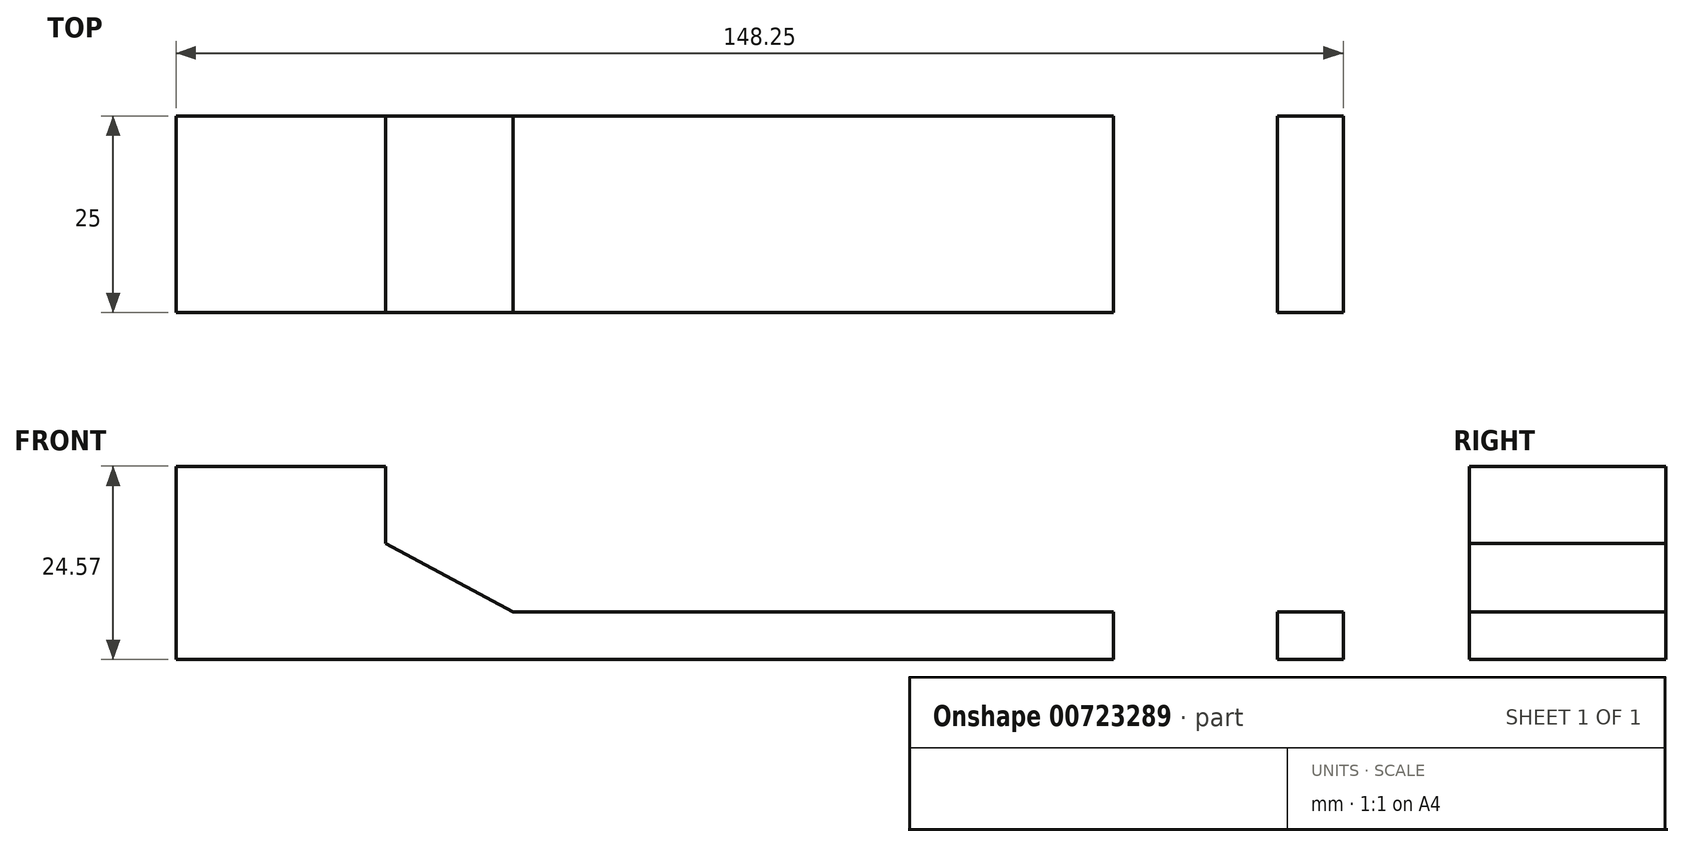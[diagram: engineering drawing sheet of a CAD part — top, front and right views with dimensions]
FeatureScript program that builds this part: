
annotation { "Feature Type Name" : "Feature", "Feature Type Description" : "" }
export const myFeature = defineFeature(function(context is Context, id is Id, definition is map)
    precondition{}
    {
        {
            var Q0;
            Q0=qCreatedBy(makeId("Front.planeOp"),FACE);
            var sketch = newSketch(context, id + "F0", { "sketchPlane" : qUnion([Q0])});
            skLineSegment(sketch, "E0", {"start": v(-75.28, 0) * mm, "end": v(-75.28, 18.5) * mm});
            skLineSegment(sketch, "E1", {"start": v(-75.28, 18.5) * mm, "end": v(-48.7, 18.5) * mm});
            skLineSegment(sketch, "E2", {"start": v(-48.7, 18.5) * mm, "end": v(-48.7, 8.67) * mm});
            skLineSegment(sketch, "E3", {"start": v(-48.7, 8.67) * mm, "end": v(-32.51, 0) * mm});
            skLineSegment(sketch, "E4", {"start": v(-32.51, 0) * mm, "end": v(72.97, 0) * mm});
            skLineSegment(sketch, "E5", {"start": v(72.97, 0.29) * mm, "end": v(72.97, -6.07) * mm});
            skLineSegment(sketch, "E6", {"start": v(72.97, -6.07) * mm, "end": v(64.59, -6.07) * mm});
            skLineSegment(sketch, "E7", {"start": v(64.59, -6.07) * mm, "end": v(64.59, 0) * mm});
            skLineSegment(sketch, "E8", {"start": v(64.59, 0) * mm, "end": v(43.78, 0) * mm});
            skLineSegment(sketch, "E9", {"start": v(43.78, 0) * mm, "end": v(43.78, -6.07) * mm});
            skLineSegment(sketch, "E10", {"start": v(43.78, -6.07) * mm, "end": v(-75.28, -6.07) * mm});
            skLineSegment(sketch, "E11", {"start": v(-75.28, -6.07) * mm, "end": v(-75.28, 0) * mm});
            skLineSegment(sketch, "E12", {"start": v(-74.7, -0.87) * mm, "end": v(-32.51, 0) * mm});
            skCircle(sketch, "E13", {"center": v(58.8, -3.76) * mm, "radius": 3.48 * mm});
            skCircle(sketch, "E14", {"center": v(58.8, -12.14) * mm, "radius": 8.38 * mm});
            skSolve(sketch);
        }
        {
            var Q0;
            Q0=makeQuery(id+"F0.imprint","IMPRINT",FACE,{"disambiguationData":[TD([[makeQuery(id+"F0.imprint","IMPRINT",EDGE,{"derivedFrom":sQuery(id+"F0.wireOp",EDGE,"E0")}),-1.0]])]});
            var Q1;
            {var subQ4=sQuery(id+"F0.wireOp",EDGE,"E6");Q1=makeQuery(id+"F0.imprint","IMPRINT",FACE,{"disambiguationData":[TD([[makeQuery(id+"F0.imprint","IMPRINT",EDGE,{"derivedFrom":subQ4}),-1.0]])]});}
            extrude(context, id + "F1", {"entities" : qUnion([Q0, Q1]), "depth" : 25 * mm, "offsetDistance" : 25 * mm});
        }
    });
